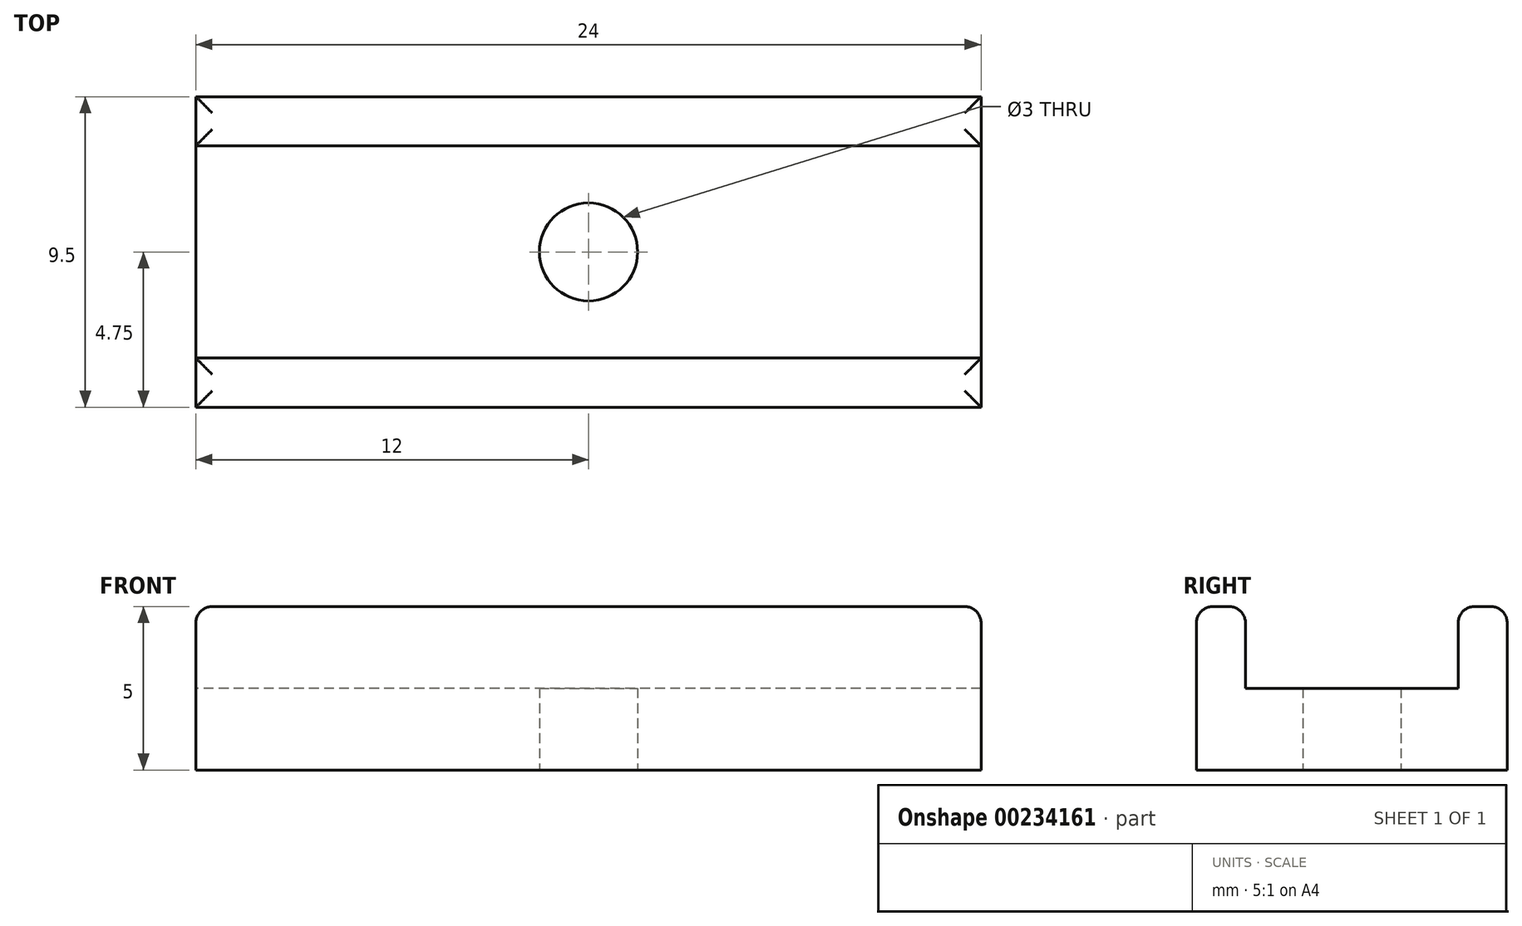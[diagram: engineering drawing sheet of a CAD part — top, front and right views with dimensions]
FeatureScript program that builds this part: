
annotation { "Feature Type Name" : "Feature", "Feature Type Description" : "" }
export const myFeature = defineFeature(function(context is Context, id is Id, definition is map)
    precondition{}
    {
        {
            var Q0;
            Q0=qCreatedBy(makeId("Right.planeOp"),FACE);
            var sketch = newSketch(context, id + "F0", { "sketchPlane" : qUnion([Q0]), "asVersion" : FeatureScriptVersionNumber.V376_FS_VERSION_BUMP});
            skLineSegment(sketch, "E0.bottom", {"start": v(-4.75, 5) * mm, "end": v(-3.25, 5) * mm});
            skLineSegment(sketch, "E0.top", {"start": v(-4.75, 0) * mm, "end": v(4.75, 0) * mm});
            skLineSegment(sketch, "E0.left", {"start": v(-4.75, 5) * mm, "end": v(-4.75, 0) * mm});
            skLineSegment(sketch, "E0.right", {"start": v(4.75, 5) * mm, "end": v(4.75, 0) * mm});
            skLineSegment(sketch, "E1.top", {"start": v(-3.25, 2.5) * mm, "end": v(3.25, 2.5) * mm});
            skLineSegment(sketch, "E1.left", {"start": v(-3.25, 5) * mm, "end": v(-3.25, 2.5) * mm});
            skLineSegment(sketch, "E1.right", {"start": v(3.25, 5) * mm, "end": v(3.25, 2.5) * mm});
            skLineSegment(sketch, "E2.trimOffspring", {"start": v(3.25, 5) * mm, "end": v(4.75, 5) * mm});
            skSolve(sketch);
        }
        {
            var Q0;
            Q0=makeQuery(id+"F0.imprint","IMPRINT",FACE,{"disambiguationData":[TD([[makeQuery(id+"F0.imprint","IMPRINT",EDGE,{"derivedFrom":sQuery(id+"F0.wireOp",EDGE,"E0.bottom")}),-1.0]])]});
            extrude(context, id + "F1", {"entities" : qUnion([Q0]), "depth" : 24 * mm});
        }
        {
            var Q0;
            Q0=makeQuery(id+"F1.opExtrude","SWEPT_FACE",FACE,{"disambiguationData":[OSD([sQuery(id+"F0.wireOp",EDGE,"E1.top")])]});
            var sketch = newSketch(context, id + "F2", { "sketchPlane" : qUnion([Q0]), "asVersion" : FeatureScriptVersionNumber.V376_FS_VERSION_BUMP});
            skPoint(sketch, "E3", {"position": v(12, 0) * mm});
            skPoint(sketch, "E3.positionSnap0", {"position": v(12, 3.25) * mm});
            skSolve(sketch);
        }
        {
            var Q0;
            Q0=sQuery(id+"F2.wireOp",VERTEX,"E3");
            var Q1;
            Q1=makeQuery(id+"F1.opExtrude","SWEPT_BODY",BODY,{"disambiguationData":[OSD([sQuery(id+"F0.wireOp",EDGE,"E0.bottom"),sQuery(id+"F0.wireOp",EDGE,"E0.top"),sQuery(id+"F0.wireOp",EDGE,"E0.left"),sQuery(id+"F0.wireOp",EDGE,"E0.right"),sQuery(id+"F0.wireOp",EDGE,"E1.top"),sQuery(id+"F0.wireOp",EDGE,"E1.left"),sQuery(id+"F0.wireOp",EDGE,"E1.right"),sQuery(id+"F0.wireOp",EDGE,"E2.trimOffspring")])]});
            hole(context, id + "F3", {"style" : HoleStyle.SIMPLE, "endStyle" : HoleEndStyle.THROUGH, "holeDiameter" : 3 * mm, "locations" : qUnion([Q0]), "scope" : qUnion([Q1]), "isTappedThrough" : true, "startStyle" : HoleStartStyle.PART});
        }
        {
            var Q0;
            Q0=makeQuery(id+"F1.opExtrude","SWEPT_EDGE",EDGE,{"disambiguationData":[OSD([sQuery(id+"F0.wireOp",EDGE,"E1.right"),sQuery(id+"F0.wireOp",EDGE,"E2.trimOffspring")])]});
            var Q1;
            Q1=makeQuery(id+"F1.opExtrude","SWEPT_EDGE",EDGE,{"disambiguationData":[OSD([sQuery(id+"F0.wireOp",EDGE,"E0.bottom"),sQuery(id+"F0.wireOp",EDGE,"E1.left")])]});
            var Q2;
            Q2=makeQuery(id+"F1.opExtrude","SWEPT_EDGE",EDGE,{"disambiguationData":[OSD([sQuery(id+"F0.wireOp",EDGE,"E0.bottom"),sQuery(id+"F0.wireOp",EDGE,"E0.left")])]});
            var Q3;
            Q3=makeQuery(id+"F1.opExtrude","SWEPT_EDGE",EDGE,{"disambiguationData":[OSD([sQuery(id+"F0.wireOp",EDGE,"E0.right"),sQuery(id+"F0.wireOp",EDGE,"E2.trimOffspring")])]});
            var Q4;
            Q4=makeQuery(id+"F1.opExtrude","CAP_EDGE",EDGE,{"disambiguationData":[OSD([sQuery(id+"F0.wireOp",EDGE,"E2.trimOffspring")])],"isStart":true});
            var Q5;
            Q5=makeQuery(id+"F1.opExtrude","CAP_EDGE",EDGE,{"disambiguationData":[OSD([sQuery(id+"F0.wireOp",EDGE,"E0.bottom")])],"isStart":true});
            var Q6;
            Q6=makeQuery(id+"F1.opExtrude","CAP_EDGE",EDGE,{"disambiguationData":[OSD([sQuery(id+"F0.wireOp",EDGE,"E0.bottom")])],"isStart":false});
            var Q7;
            Q7=makeQuery(id+"F1.opExtrude","CAP_EDGE",EDGE,{"disambiguationData":[OSD([sQuery(id+"F0.wireOp",EDGE,"E2.trimOffspring")])],"isStart":false});
            fillet(context, id + "F4", {"entities" : qUnion([Q0, Q1, Q2, Q3, Q4, Q5, Q6, Q7]), "radius" : 0.5 * mm, "tangentPropagation" : true, "allowEdgeOverflow" : false});
        }
    });
